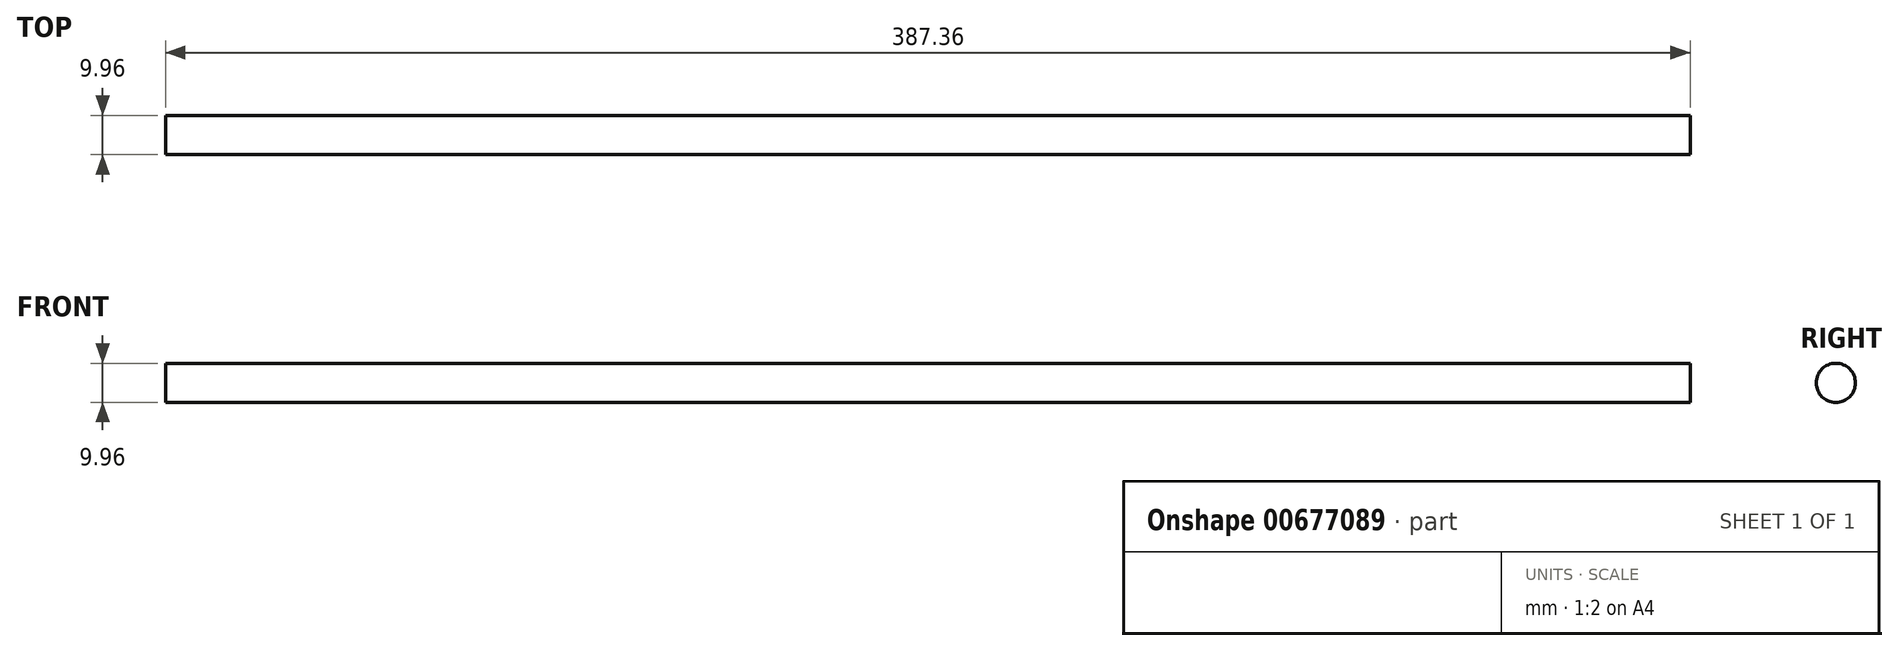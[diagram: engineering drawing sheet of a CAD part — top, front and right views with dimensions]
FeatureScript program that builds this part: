
annotation { "Feature Type Name" : "Feature", "Feature Type Description" : "" }
export const myFeature = defineFeature(function(context is Context, id is Id, definition is map)
    precondition{}
    {
        {
            var Q0;
            Q0=qCreatedBy(makeId("Right.planeOp"),FACE);
            var sketch = newSketch(context, id + "F0", { "sketchPlane" : qUnion([Q0])});
            skCircle(sketch, "E0", {"center": v(0, 0) * mm, "radius": 4.98 * mm});
            skSolve(sketch);
        }
        {
            var Q0;
            Q0 = qSketchRegion(id + "F0", true);
            extrude(context, id + "F1", {"entities" : qUnion([Q0]), "endBound" : BoundingType.SYMMETRIC, "depth" : 387.35 * mm, "offsetDistance" : 25.4 * mm});
        }
    });
